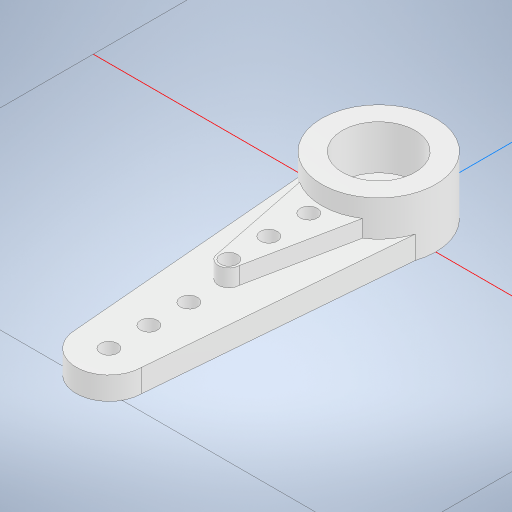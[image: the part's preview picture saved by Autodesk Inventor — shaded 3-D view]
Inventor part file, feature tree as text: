
AUTODESK INVENTOR PART (.ipt)
format: ipt  version: 2023 (Build 270158000, 158)  size: 302,592 bytes
history: native  units: mm
features: extrude x5, sketch x1
ambient origin geometry x8: Origin, YZ Plane, XZ Plane, XY Plane, X Axis, Y Axis, Z Axis, Center Point
bodies: Volumenkörper1 (feature_tree)
feature tree (6):
  sketch  "Skizze1"  dims[d0=8.0mm d2=2.5mm d4=25.2mm d5=2.3mm d6=1.2mm d7=2.8mm d10=1.2mm d11=2.8mm d12=1.2mm d13=2.8mm d14=1.2mm d15=2.8mm d16=1.2mm d17=2.8mm d18=1.2mm d19=1.5mm d20=5.9mm d21=5.1mm d22=1.6mm d23=0.0mm d24=2.8mm d25=0.0mm d26=4.1mm d27=0.0mm d28=1.0mm d29=0.0mm d30=0.5mm d31=0.0mm]
  extrude  "Extrusion1"  Depth=2.5mm
  extrude  "Extrusion2"  Depth=0.5mm
  extrude  "Extrusion3"  Depth=2.3mm
  extrude  "Extrusion4"  Depth=1.2mm
  extrude  "Extrusion5"  Depth=2.8mm
